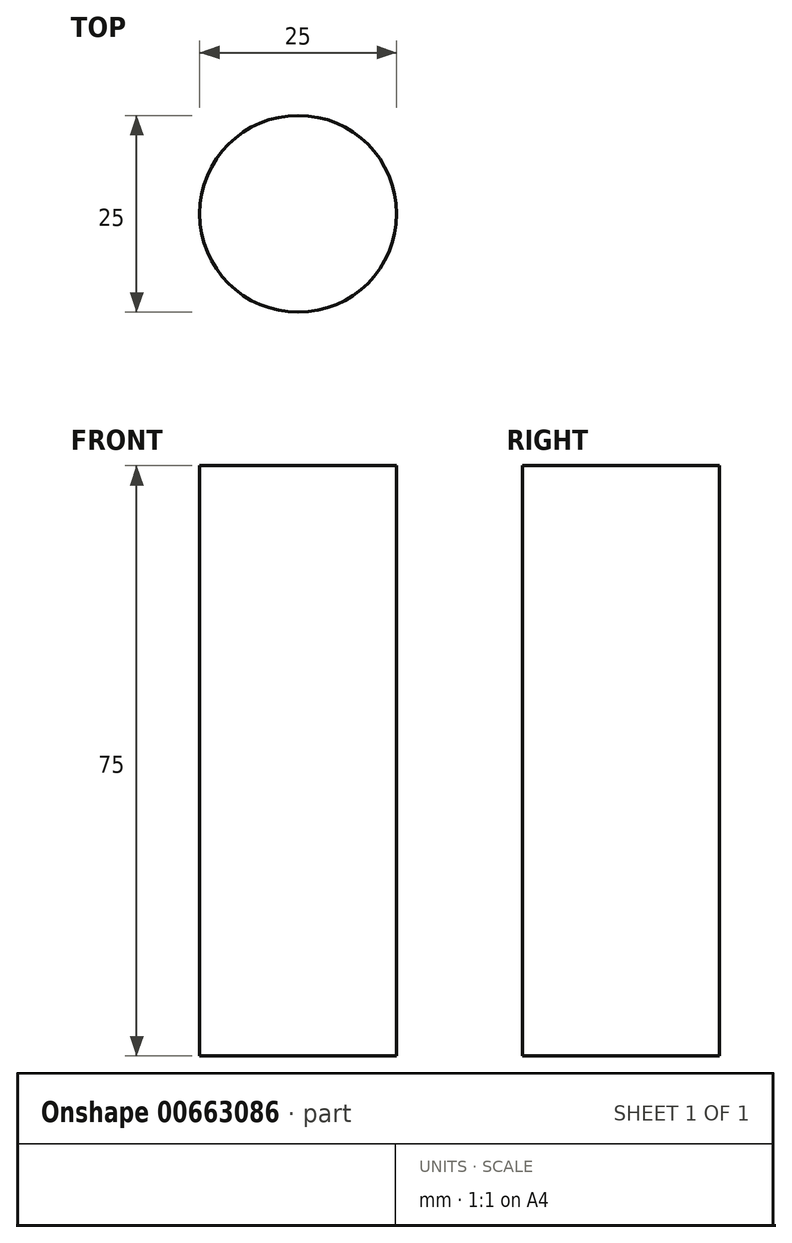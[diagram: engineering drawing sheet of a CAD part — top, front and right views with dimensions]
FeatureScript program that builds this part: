
annotation { "Feature Type Name" : "Feature", "Feature Type Description" : "" }
export const myFeature = defineFeature(function(context is Context, id is Id, definition is map)
    precondition{}
    {
        {
            var Q0;
            Q0=qCreatedBy(makeId("Top.planeOp"),FACE);
            var sketch = newSketch(context, id + "F0", { "sketchPlane" : qUnion([Q0])});
            skCircle(sketch, "E0", {"center": v(0, 0) * mm, "radius": 12.5 * mm});
            skSolve(sketch);
        }
        {
            var Q0;
            Q0=makeQuery(id+"F0.imprint","IMPRINT",FACE,{"disambiguationData":[TD([[makeQuery(id+"F0.imprint","IMPRINT",EDGE,{"derivedFrom":sQuery(id+"F0.wireOp",EDGE,"E0")}),1.0]])]});
            extrude(context, id + "F1", {"entities" : qUnion([Q0]), "depth" : 75 * mm, "offsetDistance" : 25 * mm});
        }
    });
